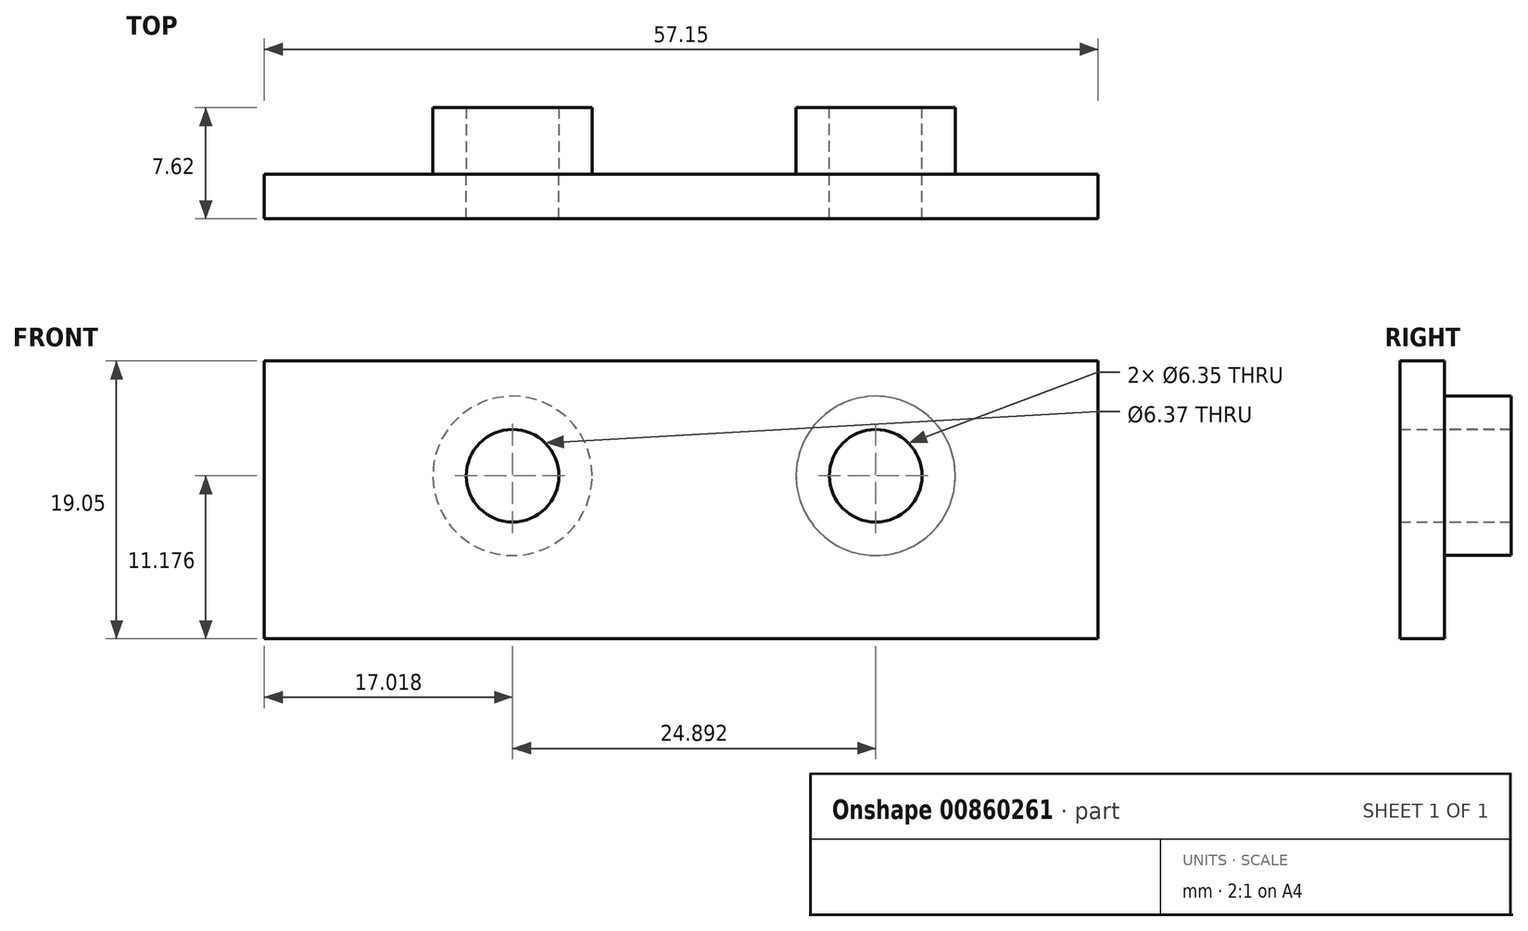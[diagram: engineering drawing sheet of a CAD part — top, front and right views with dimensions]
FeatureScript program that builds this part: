
annotation { "Feature Type Name" : "Feature", "Feature Type Description" : "" }
export const myFeature = defineFeature(function(context is Context, id is Id, definition is map)
    precondition{}
    {
        {
            var Q0;
            Q0=qCreatedBy(makeId("Front.planeOp"),FACE);
            var sketch = newSketch(context, id + "F0", { "sketchPlane" : qUnion([Q0])});
            skLineSegment(sketch, "E0.bottom", {"start": v(-57.15, 19.05) * mm, "end": v(0, 19.05) * mm});
            skLineSegment(sketch, "E0.top", {"start": v(-57.15, 0) * mm, "end": v(0, 0) * mm});
            skLineSegment(sketch, "E0.left", {"start": v(-57.15, 19.05) * mm, "end": v(-57.15, 0) * mm});
            skLineSegment(sketch, "E0.right", {"start": v(0, 19.05) * mm, "end": v(0, 0) * mm});
            skCircle(sketch, "E1", {"center": v(-15.24, 11.18) * mm, "radius": 3.18 * mm});
            skCircle(sketch, "E2", {"center": v(-40.13, 11.18) * mm, "radius": 3.18 * mm});
            skSolve(sketch);
        }
        {
            var Q0;
            Q0=makeQuery(id+"F0.imprint","IMPRINT",FACE,{"disambiguationData":[TD([[makeQuery(id+"F0.imprint","IMPRINT",EDGE,{"derivedFrom":sQuery(id+"F0.wireOp",EDGE,"E0.bottom")}),-1.0]])]});
            extrude(context, id + "F1", {"entities" : qUnion([Q0]), "depth" : 3.05 * mm, "offsetDistance" : 25.4 * mm});
        }
        {
            var Q0;
            Q0=makeQuery(id+"F1.opExtrude","CAP_FACE",FACE,{"disambiguationData":[OSD([sQuery(id+"F0.wireOp",EDGE,"E0.bottom"),sQuery(id+"F0.wireOp",EDGE,"E0.top"),sQuery(id+"F0.wireOp",EDGE,"E0.left"),sQuery(id+"F0.wireOp",EDGE,"E0.right"),sQuery(id+"F0.wireOp",EDGE,"E1"),sQuery(id+"F0.wireOp",EDGE,"E2")])],"isStart":true});
            var sketch = newSketch(context, id + "F2", { "sketchPlane" : qUnion([Q0])});
            skCircle(sketch, "E3", {"center": v(15.24, 11.18) * mm, "radius": 3.12 * mm});
            skCircle(sketch, "E4", {"center": v(40.13, 11.18) * mm, "radius": 3.18 * mm});
            skCircle(sketch, "E5", {"center": v(15.24, 11.18) * mm, "radius": 5.46 * mm});
            skCircle(sketch, "E6", {"center": v(40.13, 11.18) * mm, "radius": 5.46 * mm});
            skSolve(sketch);
        }
        {
            var Q0;
            Q0=makeQuery(id+"F2.imprint","IMPRINT",FACE,{"disambiguationData":[TD([[makeQuery(id+"F2.imprint","IMPRINT",EDGE,{"derivedFrom":sQuery(id+"F2.wireOp",EDGE,"E5")}),1.0]])]});
            var Q1;
            Q1=makeQuery(id+"F2.imprint","IMPRINT",FACE,{"disambiguationData":[TD([[makeQuery(id+"F2.imprint","IMPRINT",EDGE,{"derivedFrom":sQuery(id+"F2.wireOp",EDGE,"E4")}),-1.0]])]});
            extrude(context, id + "F3", {"entities" : qUnion([Q0, Q1]), "operationType" : NewBodyOperationType.ADD, "depth" : 4.57 * mm, "offsetDistance" : 25.4 * mm});
        }
    });
